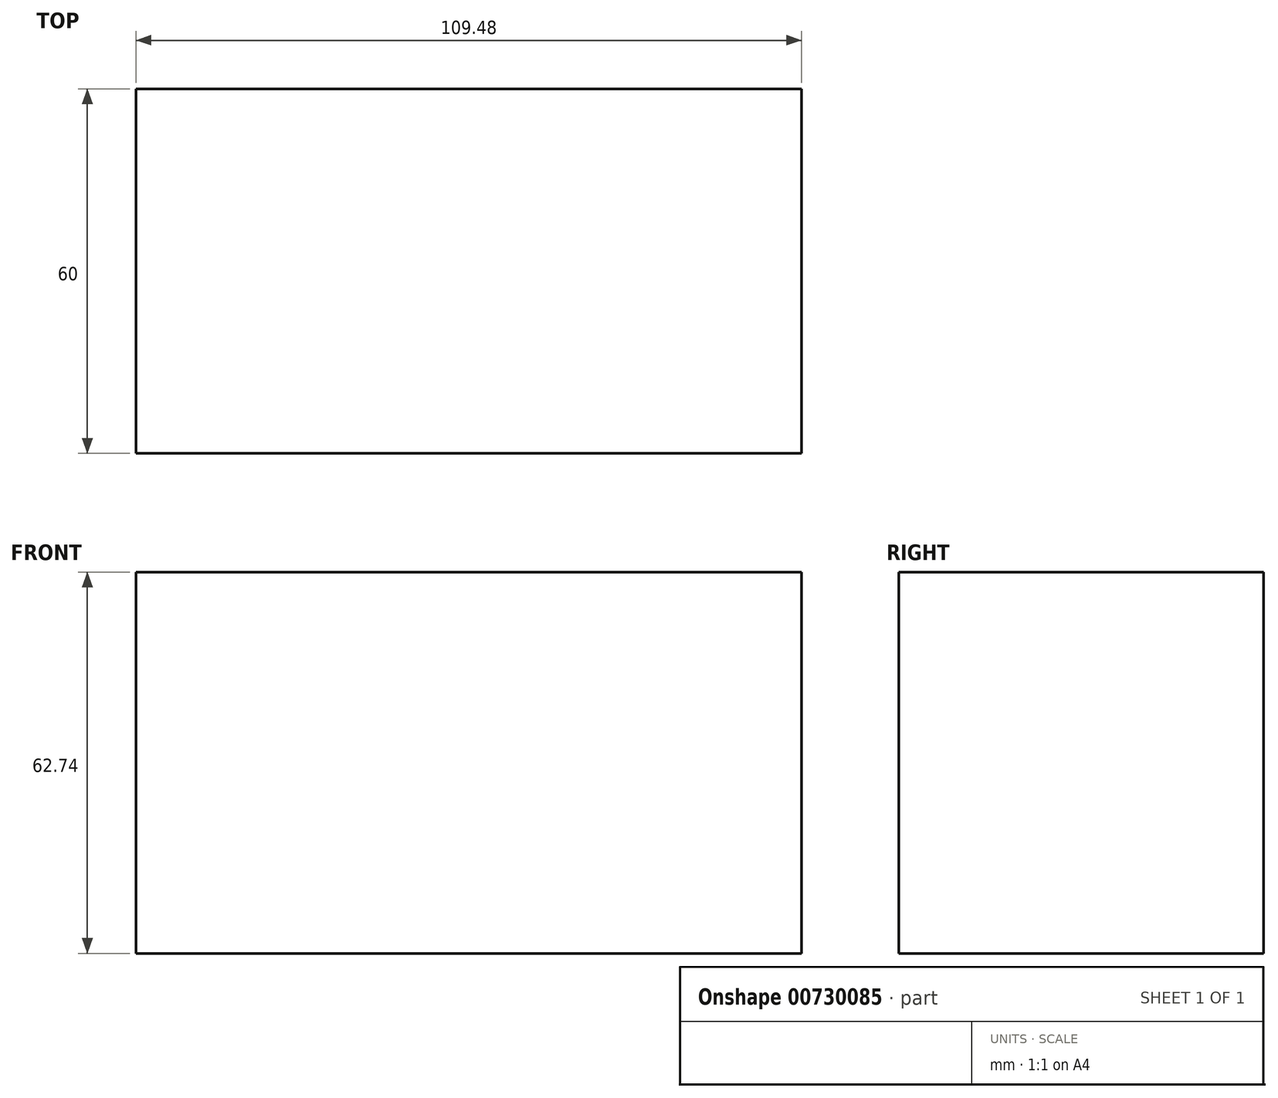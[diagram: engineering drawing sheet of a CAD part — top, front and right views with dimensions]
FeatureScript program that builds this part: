
annotation { "Feature Type Name" : "Feature", "Feature Type Description" : "" }
export const myFeature = defineFeature(function(context is Context, id is Id, definition is map)
    precondition{}
    {
        {
            var Q0;
            Q0=qCreatedBy(makeId("Front.planeOp"),FACE);
            var sketch = newSketch(context, id + "F0", { "sketchPlane" : qUnion([Q0])});
            skLineSegment(sketch, "E0.bottom", {"start": v(54.74, 31.37) * mm, "end": v(-54.74, 31.37) * mm});
            skLineSegment(sketch, "E0.top", {"start": v(54.74, -31.37) * mm, "end": v(-54.74, -31.37) * mm});
            skLineSegment(sketch, "E0.left", {"start": v(54.74, 31.37) * mm, "end": v(54.74, -31.37) * mm});
            skLineSegment(sketch, "E0.right", {"start": v(-54.74, 31.37) * mm, "end": v(-54.74, -31.37) * mm});
            skPoint(sketch, "E0.middle", {"position": v(0, 0) * mm});
            skSolve(sketch);
        }
        {
            var Q0;
            Q0 = qSketchRegion(id + "F0", true);
            extrude(context, id + "F1", {"entities" : qUnion([Q0]), "endBound" : BoundingType.SYMMETRIC, "depth" : 60 * mm, "offsetDistance" : 25.4 * mm});
        }
        {
            var Q0;
            Q0=makeQuery(id+"F1.opExtrude","SWEPT_FACE",FACE,{"disambiguationData":[OSD([sQuery(id+"F0.wireOp",EDGE,"E0.bottom")])]});
            var sketch = newSketch(context, id + "F2", { "sketchPlane" : qUnion([Q0])});
            skCircle(sketch, "E1", {"center": v(0, 0) * mm, "radius": 15.18 * mm});
            skSolve(sketch);
        }
        {
            var Q0;
            Q0=makeQuery(id+"F2.imprint","IMPRINT",FACE,{"disambiguationData":[TD([[makeQuery(id+"F2.imprint","IMPRINT",EDGE,{"derivedFrom":sQuery(id+"F2.wireOp",EDGE,"E1")}),1.0]])]});
            extrude(context, id + "F3", {"entities" : qUnion([Q0]), "operationType" : NewBodyOperationType.ADD, "oppositeDirection" : true, "depth" : 50.8 * mm, "offsetDistance" : 25.4 * mm});
        }
    });
